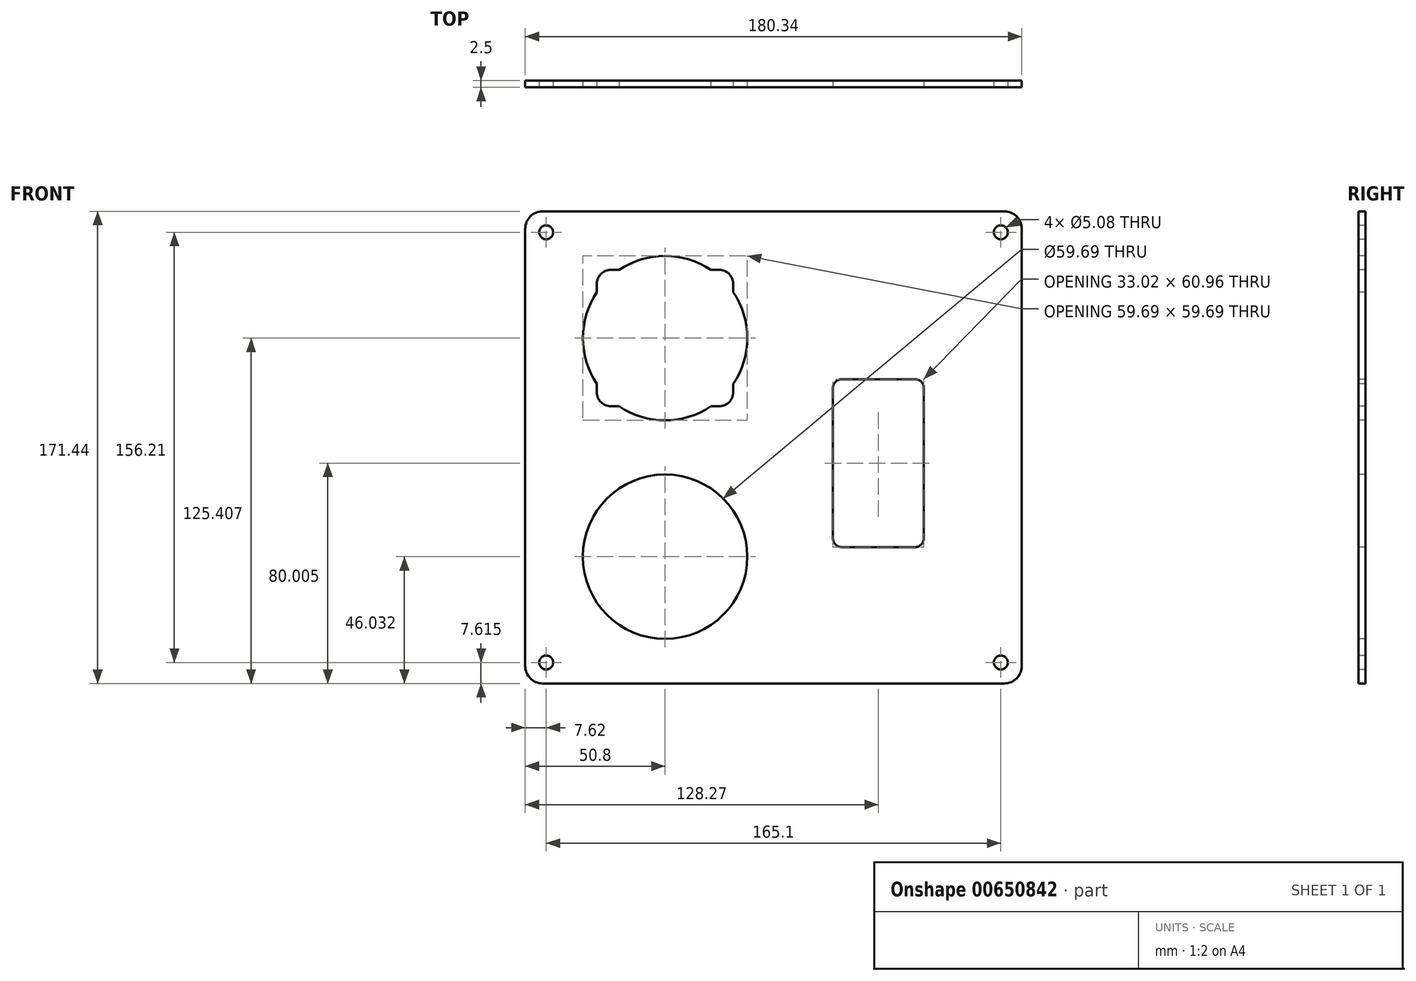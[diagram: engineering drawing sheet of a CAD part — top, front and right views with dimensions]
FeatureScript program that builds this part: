
annotation { "Feature Type Name" : "Feature", "Feature Type Description" : "" }
export const myFeature = defineFeature(function(context is Context, id is Id, definition is map)
    precondition{}
    {
        {
            var Q0;
            Q0=qCreatedBy(makeId("Front.planeOp"),FACE);
            var sketch = newSketch(context, id + "F0", { "sketchPlane" : qUnion([Q0])});
            skLineSegment(sketch, "E0.bottom", {"start": v(83.82, 85.73) * mm, "end": v(-83.82, 85.73) * mm});
            skLineSegment(sketch, "E0.top", {"start": v(83.82, -85.73) * mm, "end": v(-83.82, -85.73) * mm});
            skLineSegment(sketch, "E0.left", {"start": v(90.17, 79.38) * mm, "end": v(90.17, -79.38) * mm});
            skLineSegment(sketch, "E0.right", {"start": v(-90.17, 79.38) * mm, "end": v(-90.17, -79.38) * mm});
            skPoint(sketch, "E0.middle", {"position": v(0, 0) * mm});
            skPoint(sketch, "E1.visualSharp", {"position": v(-90.17, 85.73) * mm});
            skArc(sketch, "E1.filletArc", {"start": v(-83.82, 85.73) * mm, "mid": v(-88.31, 83.87) * mm, "end": v(-90.17, 79.38) * mm});
            skPoint(sketch, "E2.visualSharp", {"position": v(90.17, 85.73) * mm});
            skArc(sketch, "E2.filletArc", {"start": v(90.17, 79.38) * mm, "mid": v(88.31, 83.87) * mm, "end": v(83.82, 85.73) * mm});
            skPoint(sketch, "E3.visualSharp", {"position": v(90.17, -85.73) * mm});
            skArc(sketch, "E3.filletArc", {"start": v(83.82, -85.73) * mm, "mid": v(88.31, -83.87) * mm, "end": v(90.17, -79.38) * mm});
            skPoint(sketch, "E4.visualSharp", {"position": v(-90.17, -85.73) * mm});
            skArc(sketch, "E4.filletArc", {"start": v(-90.17, -79.38) * mm, "mid": v(-88.31, -83.87) * mm, "end": v(-83.82, -85.73) * mm});
            skSolve(sketch);
        }
        {
            var Q0;
            Q0 = qSketchRegion(id + "F0", true);
            extrude(context, id + "F1", {"entities" : qUnion([Q0]), "depth" : 2.5 * mm, "offsetDistance" : 25.4 * mm});
        }
        {
            var Q0;
            Q0=makeQuery(id+"F1.opExtrude","CAP_FACE",FACE,{"disambiguationData":[OSD([sQuery(id+"F0.wireOp",EDGE,"E0.bottom"),sQuery(id+"F0.wireOp",EDGE,"E0.top"),sQuery(id+"F0.wireOp",EDGE,"E0.left"),sQuery(id+"F0.wireOp",EDGE,"E0.right"),sQuery(id+"F0.wireOp",EDGE,"E1.filletArc"),sQuery(id+"F0.wireOp",EDGE,"E2.filletArc"),sQuery(id+"F0.wireOp",EDGE,"E3.filletArc"),sQuery(id+"F0.wireOp",EDGE,"E4.filletArc")])],"isStart":false});
            var sketch = newSketch(context, id + "F2", { "sketchPlane" : qUnion([Q0])});
            skLineSegment(sketch, "E5.bottom", {"start": v(24.77, 24.77) * mm, "end": v(51.44, 24.77) * mm});
            skLineSegment(sketch, "E5.top", {"start": v(24.77, -36.2) * mm, "end": v(51.44, -36.2) * mm});
            skLineSegment(sketch, "E5.left", {"start": v(21.59, 21.6) * mm, "end": v(21.59, -33.02) * mm});
            skLineSegment(sketch, "E5.right", {"start": v(54.61, 21.6) * mm, "end": v(54.61, -33.02) * mm});
            skPoint(sketch, "E6.visualSharp", {"position": v(54.61, 24.77) * mm});
            skArc(sketch, "E6.filletArc", {"start": v(54.61, 21.6) * mm, "mid": v(53.68, 23.84) * mm, "end": v(51.44, 24.77) * mm});
            skPoint(sketch, "E7.visualSharp", {"position": v(21.59, 24.77) * mm});
            skArc(sketch, "E7.filletArc", {"start": v(24.77, 24.77) * mm, "mid": v(22.52, 23.84) * mm, "end": v(21.59, 21.6) * mm});
            skPoint(sketch, "E8.visualSharp", {"position": v(21.59, -36.2) * mm});
            skArc(sketch, "E8.filletArc", {"start": v(21.59, -33.02) * mm, "mid": v(22.52, -35.27) * mm, "end": v(24.77, -36.2) * mm});
            skPoint(sketch, "E9.visualSharp", {"position": v(54.61, -36.2) * mm});
            skArc(sketch, "E9.filletArc", {"start": v(51.44, -36.2) * mm, "mid": v(53.68, -35.27) * mm, "end": v(54.61, -33.02) * mm});
            skSolve(sketch);
        }
        {
            var Q0;
            Q0 = qSketchRegion(id + "F2", true);
            extrude(context, id + "F3", {"entities" : qUnion([Q0]), "operationType" : NewBodyOperationType.REMOVE, "oppositeDirection" : true, "depth" : 25.4 * mm, "offsetDistance" : 25.4 * mm});
        }
        {
            var Q0;
            Q0=makeQuery(id+"F1.opExtrude","CAP_FACE",FACE,{"disambiguationData":[OSD([sQuery(id+"F0.wireOp",EDGE,"E0.bottom"),sQuery(id+"F0.wireOp",EDGE,"E0.top"),sQuery(id+"F0.wireOp",EDGE,"E0.left"),sQuery(id+"F0.wireOp",EDGE,"E0.right"),sQuery(id+"F0.wireOp",EDGE,"E1.filletArc"),sQuery(id+"F0.wireOp",EDGE,"E2.filletArc"),sQuery(id+"F0.wireOp",EDGE,"E3.filletArc"),sQuery(id+"F0.wireOp",EDGE,"E4.filletArc")])],"isStart":false});
            var sketch = newSketch(context, id + "F4", { "sketchPlane" : qUnion([Q0])});
            skCircle(sketch, "E10", {"center": v(-39.37, 39.69) * mm, "radius": 29.85 * mm});
            skCircle(sketch, "E11", {"center": v(-39.37, -39.69) * mm, "radius": 29.85 * mm});
            skLineSegment(sketch, "E12.bottom", {"start": v(-14.6, 14.92) * mm, "end": v(-64.13, 14.92) * mm});
            skLineSegment(sketch, "E12.top", {"start": v(-14.6, 64.45) * mm, "end": v(-64.13, 64.45) * mm});
            skLineSegment(sketch, "E12.left", {"start": v(-14.6, 14.92) * mm, "end": v(-14.6, 64.45) * mm});
            skLineSegment(sketch, "E12.right", {"start": v(-64.14, 14.92) * mm, "end": v(-64.13, 64.45) * mm});
            skSolve(sketch);
        }
        {
            var Q0;
            Q0 = qSketchRegion(id + "F4", true);
            extrude(context, id + "F5", {"entities" : qUnion([Q0]), "operationType" : NewBodyOperationType.REMOVE, "oppositeDirection" : true, "depth" : 25.4 * mm, "offsetDistance" : 25.4 * mm});
        }
        {
            var Q0;
            Q0=makeQuery(id+"F4.imprint","IMPRINT",FACE,{"disambiguationData":[TD([[makeQuery(id+"F4.imprint","IMPRINT",EDGE,{"derivedFrom":sQuery(id+"F4.wireOp",EDGE,"E10")}),-1.0]])]});
            var sketch = newSketch(context, id + "F6", { "sketchPlane" : qUnion([Q0])});
            skCircle(sketch, "E13", {"center": v(-82.55, 78.1) * mm, "radius": 2.54 * mm});
            skCircle(sketch, "E14", {"center": v(82.55, 78.1) * mm, "radius": 2.54 * mm});
            skCircle(sketch, "E15", {"center": v(82.55, -78.1) * mm, "radius": 2.54 * mm});
            skCircle(sketch, "E16", {"center": v(-82.55, -78.1) * mm, "radius": 2.54 * mm});
            skSolve(sketch);
        }
        {
            var Q0;
            Q0 = qSketchRegion(id + "F6", true);
            extrude(context, id + "F7", {"entities" : qUnion([Q0]), "operationType" : NewBodyOperationType.REMOVE, "oppositeDirection" : true, "depth" : 25.4 * mm, "offsetDistance" : 25.4 * mm});
        }
        {
            var Q0;
            Q0=makeQuery(id+"F5.boolean.opBoolean","COPY",EDGE,{"derivedFrom":makeQuery(id+"F5.opExtrude","SWEPT_EDGE",EDGE,{"disambiguationData":[OSD([sQuery(id+"F4.wireOp",EDGE,"E12.bottom"),sQuery(id+"F4.wireOp",EDGE,"E12.right")])]})});
            var Q1;
            Q1=makeQuery(id+"F5.boolean.opBoolean","COPY",EDGE,{"derivedFrom":makeQuery(id+"F5.opExtrude","SWEPT_EDGE",EDGE,{"disambiguationData":[OSD([sQuery(id+"F4.wireOp",EDGE,"E12.bottom"),sQuery(id+"F4.wireOp",EDGE,"E12.left")])]})});
            var Q2;
            Q2=makeQuery(id+"F5.boolean.opBoolean","COPY",EDGE,{"derivedFrom":makeQuery(id+"F5.opExtrude","SWEPT_EDGE",EDGE,{"disambiguationData":[OSD([sQuery(id+"F4.wireOp",EDGE,"E12.top"),sQuery(id+"F4.wireOp",EDGE,"E12.left")])]})});
            var Q3;
            Q3=makeQuery(id+"F5.boolean.opBoolean","COPY",EDGE,{"derivedFrom":makeQuery(id+"F5.opExtrude","SWEPT_EDGE",EDGE,{"disambiguationData":[OSD([sQuery(id+"F4.wireOp",EDGE,"E12.top"),sQuery(id+"F4.wireOp",EDGE,"E12.right")])]})});
            fillet(context, id + "F8", {"entities" : qUnion([Q0, Q1, Q2, Q3]), "radius" : 5.08 * mm, "tangentPropagation" : true, "allowEdgeOverflow" : false});
        }
    });
